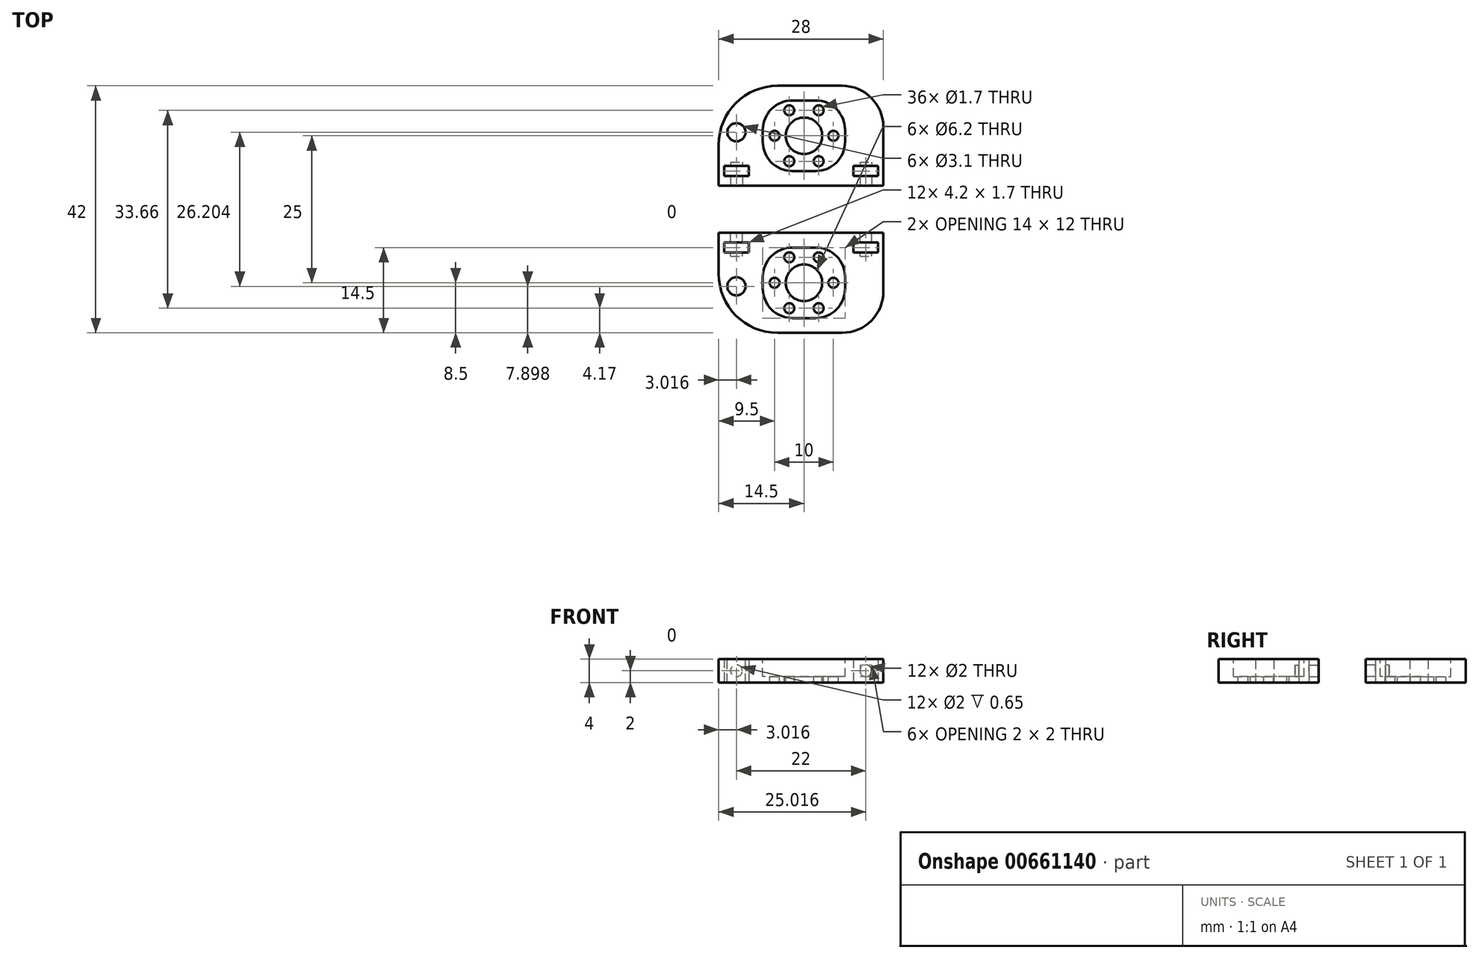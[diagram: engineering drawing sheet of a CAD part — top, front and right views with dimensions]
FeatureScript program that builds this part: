
annotation { "Feature Type Name" : "Feature", "Feature Type Description" : "" }
export const myFeature = defineFeature(function(context is Context, id is Id, definition is map)
    precondition{}
    {
        {
            var Q0;
            Q0=qCreatedBy(makeId("Front.planeOp"),FACE);
            var sketch = newSketch(context, id + "F0", { "sketchPlane" : qUnion([Q0])});
            skLineSegment(sketch, "E0.bottom", {"start": v(0, 0) * mm, "end": v(28, 0) * mm});
            skLineSegment(sketch, "E0.top", {"start": v(0, 17) * mm, "end": v(28, 17) * mm});
            skLineSegment(sketch, "E0.left", {"start": v(0, 0) * mm, "end": v(0, 17) * mm});
            skLineSegment(sketch, "E0.right", {"start": v(28, 0) * mm, "end": v(28, 17) * mm});
            skCircle(sketch, "E1", {"center": v(14.5, 8.5) * mm, "radius": 3.1 * mm});
            skCircle(sketch, "E2", {"center": v(19.5, 8.5) * mm, "radius": 0.85 * mm});
            skCircle(sketch, "E3.1.0", {"center": v(17, 12.83) * mm, "radius": 0.85 * mm});
            skCircle(sketch, "E3.2.0", {"center": v(12, 12.83) * mm, "radius": 0.85 * mm});
            skCircle(sketch, "E3.3.0", {"center": v(9.5, 8.5) * mm, "radius": 0.85 * mm});
            skCircle(sketch, "E3.4.0", {"center": v(12, 4.17) * mm, "radius": 0.85 * mm});
            skCircle(sketch, "E3.5.0", {"center": v(17, 4.17) * mm, "radius": 0.85 * mm});
            skLineSegment(sketch, "E4.bottom", {"start": v(7.5, 14.5) * mm, "end": v(21.5, 14.5) * mm});
            skLineSegment(sketch, "E4.top", {"start": v(7.5, 2.5) * mm, "end": v(21.5, 2.5) * mm});
            skLineSegment(sketch, "E4.left", {"start": v(7.5, 14.5) * mm, "end": v(7.5, 2.5) * mm});
            skLineSegment(sketch, "E4.right", {"start": v(21.5, 14.5) * mm, "end": v(21.5, 2.5) * mm});
            skCircle(sketch, "E5", {"center": v(3.02, 9.1) * mm, "radius": 1.55 * mm});
            skLineSegment(sketch, "E6", {"start": v(3.02, 9.1) * mm, "end": v(14.5, 8.5) * mm});
            skLineSegment(sketch, "E7", {"start": v(14.5, 8.5) * mm, "end": v(0, 8.5) * mm});
            skSolve(sketch);
        }
        {
            var Q0;
            Q0=makeQuery(id+"F0.imprint","IMPRINT",FACE,{"disambiguationData":[TD([[makeQuery(id+"F0.imprint","IMPRINT",EDGE,{"derivedFrom":sQuery(id+"F0.wireOp",EDGE,"E0.bottom")}),1.0]])]});
            var Q1;
            Q1=makeQuery(id+"F0.imprint","IMPRINT",FACE,{"disambiguationData":[TD([[makeQuery(id+"F0.imprint","IMPRINT",EDGE,{"derivedFrom":sQuery(id+"F0.wireOp",EDGE,"E1")}),-1.0]])]});
            var Q2;
            Q2=makeQuery(id+"F0.imprint","IMPRINT",FACE,{"disambiguationData":[TD([[makeQuery(id+"F0.imprint","IMPRINT",EDGE,{"derivedFrom":sQuery(id+"F0.wireOp",EDGE,"E2")}),-1.0]])]});
            var Q3;
            {var subQ0=sQuery(id+"F0.wireOp",EDGE,"E6");var subQ1=sQuery(id+"F0.wireOp",EDGE,"E3.3.0");var subQ2=makeQuery(id+"F0.imprint","INTERSECT",VERTEX,{"disambiguationData":[OD(0.0)],"derivedFrom":[subQ1,subQ0]});Q3=makeQuery(id+"F0.imprint","IMPRINT",FACE,{"disambiguationData":[TD([[makeQuery(id+"F0.imprint","IMPRINT",EDGE,{"disambiguationData":[TD([[subQ2,1.0]])],"derivedFrom":subQ1}),-1.0]])]});}
            var Q4;
            {var subQ0=sQuery(id+"F0.wireOp",EDGE,"E7");var subQ1=sQuery(id+"F0.wireOp",EDGE,"E4.left");var subQ2=makeQuery(id+"F0.imprint","INTERSECT",VERTEX,{"derivedFrom":[subQ1,subQ0]});Q4=makeQuery(id+"F0.imprint","IMPRINT",FACE,{"disambiguationData":[TD([[makeQuery(id+"F0.imprint","IMPRINT",EDGE,{"disambiguationData":[TD([[subQ2,-1.0]])],"derivedFrom":subQ1}),-1.0]])]});}
            var Q5;
            {var subQ0=sQuery(id+"F0.wireOp",EDGE,"E6");var subQ1=sQuery(id+"F0.wireOp",EDGE,"E4.left");var subQ2=makeQuery(id+"F0.imprint","INTERSECT",VERTEX,{"derivedFrom":[subQ1,subQ0]});Q5=makeQuery(id+"F0.imprint","IMPRINT",FACE,{"disambiguationData":[TD([[makeQuery(id+"F0.imprint","IMPRINT",EDGE,{"disambiguationData":[TD([[subQ2,-1.0]])],"derivedFrom":subQ1}),-1.0]])]});}
            var Q6;
            {var subQ0=sQuery(id+"F0.wireOp",EDGE,"E6");var subQ1=sQuery(id+"F0.wireOp",EDGE,"E3.3.0");var subQ2=makeQuery(id+"F0.imprint","INTERSECT",VERTEX,{"disambiguationData":[OD(1.0)],"derivedFrom":[subQ1,subQ0]});Q6=makeQuery(id+"F0.imprint","IMPRINT",FACE,{"disambiguationData":[TD([[makeQuery(id+"F0.imprint","IMPRINT",EDGE,{"disambiguationData":[TD([[subQ2,-1.0]])],"derivedFrom":subQ1}),-1.0]])]});}
            extrude(context, id + "F1", {"entities" : qUnion([Q0, Q1, Q2, Q3, Q4, Q5, Q6]), "depth" : 4 * mm});
        }
        {
            var Q0;
            Q0=makeQuery(id+"F1.opExtrude","SWEPT_EDGE",EDGE,{"disambiguationData":[OSD([sQuery(id+"F0.wireOp",EDGE,"E0.top"),sQuery(id+"F0.wireOp",EDGE,"E0.left")])]});
            fillet(context, id + "F2", {"entities" : qUnion([Q0]), "radius" : 10 * mm, "tangentPropagation" : true, "allowEdgeOverflow" : false});
        }
        {
            var Q0;
            Q0=makeQuery(id+"F0.imprint","IMPRINT",FACE,{"disambiguationData":[TD([[makeQuery(id+"F0.imprint","IMPRINT",EDGE,{"derivedFrom":sQuery(id+"F0.wireOp",EDGE,"E2")}),-1.0]])]});
            var Q1;
            {var subQ0=sQuery(id+"F0.wireOp",EDGE,"E6");var subQ1=sQuery(id+"F0.wireOp",EDGE,"E1");var subQ2=makeQuery(id+"F0.imprint","INTERSECT",VERTEX,{"derivedFrom":[subQ1,subQ0]});Q1=makeQuery(id+"F0.imprint","IMPRINT",FACE,{"disambiguationData":[TD([[makeQuery(id+"F0.imprint","IMPRINT",EDGE,{"disambiguationData":[TD([[subQ2,1.0]])],"derivedFrom":subQ1}),-1.0]])]});}
            var Q2;
            {var subQ0=sQuery(id+"F0.wireOp",EDGE,"E6");var subQ1=sQuery(id+"F0.wireOp",EDGE,"E3.3.0");var subQ2=makeQuery(id+"F0.imprint","INTERSECT",VERTEX,{"disambiguationData":[OD(1.0)],"derivedFrom":[subQ1,subQ0]});Q2=makeQuery(id+"F0.imprint","IMPRINT",FACE,{"disambiguationData":[TD([[makeQuery(id+"F0.imprint","IMPRINT",EDGE,{"disambiguationData":[TD([[subQ2,-1.0]])],"derivedFrom":subQ1}),-1.0]])]});}
            var Q3;
            {var subQ0=sQuery(id+"F0.wireOp",EDGE,"E6");var subQ1=sQuery(id+"F0.wireOp",EDGE,"E1");var subQ2=makeQuery(id+"F0.imprint","INTERSECT",VERTEX,{"derivedFrom":[subQ1,subQ0]});Q3=makeQuery(id+"F0.imprint","IMPRINT",FACE,{"disambiguationData":[TD([[makeQuery(id+"F0.imprint","IMPRINT",EDGE,{"disambiguationData":[TD([[subQ2,-1.0]])],"derivedFrom":subQ1}),-1.0]])]});}
            extrude(context, id + "F3", {"entities" : qUnion([Q0, Q1, Q2, Q3]), "operationType" : NewBodyOperationType.REMOVE, "depth" : 3 * mm});
        }
        {
            var Q0;
            Q0=makeQuery(id+"F3.boolean.opBoolean","COPY",EDGE,{"derivedFrom":makeQuery(id+"F3.opExtrude","SWEPT_EDGE",EDGE,{"disambiguationData":[OSD([sQuery(id+"F0.wireOp",EDGE,"E4.bottom"),sQuery(id+"F0.wireOp",EDGE,"E4.right")])]})});
            var Q1;
            Q1=makeQuery(id+"F3.boolean.opBoolean","COPY",EDGE,{"derivedFrom":makeQuery(id+"F3.opExtrude","SWEPT_EDGE",EDGE,{"disambiguationData":[OSD([sQuery(id+"F0.wireOp",EDGE,"E4.top"),sQuery(id+"F0.wireOp",EDGE,"E4.right")])]})});
            var Q2;
            Q2=makeQuery(id+"F3.boolean.opBoolean","COPY",EDGE,{"derivedFrom":makeQuery(id+"F3.opExtrude","SWEPT_EDGE",EDGE,{"disambiguationData":[OSD([sQuery(id+"F0.wireOp",EDGE,"E4.top"),sQuery(id+"F0.wireOp",EDGE,"E4.left")])]})});
            var Q3;
            Q3=makeQuery(id+"F3.boolean.opBoolean","COPY",EDGE,{"derivedFrom":makeQuery(id+"F3.opExtrude","SWEPT_EDGE",EDGE,{"disambiguationData":[OSD([sQuery(id+"F0.wireOp",EDGE,"E4.bottom"),sQuery(id+"F0.wireOp",EDGE,"E4.left")])]})});
            fillet(context, id + "F4", {"entities" : qUnion([Q0, Q1, Q2, Q3]), "radius" : 5 * mm, "tangentPropagation" : true, "allowEdgeOverflow" : false});
        }
        {
            var Q0;
            Q0=makeQuery(id+"F1.opExtrude","SWEPT_EDGE",EDGE,{"disambiguationData":[OSD([sQuery(id+"F0.wireOp",EDGE,"E0.top"),sQuery(id+"F0.wireOp",EDGE,"E0.right")])]});
            fillet(context, id + "F5", {"entities" : qUnion([Q0]), "radius" : 7 * mm, "tangentPropagation" : true, "allowEdgeOverflow" : false});
        }
        {
            var Q0;
            Q0=makeQuery(id+"F1.opExtrude","SWEPT_FACE",FACE,{"disambiguationData":[OSD([sQuery(id+"F0.wireOp",EDGE,"E0.bottom")])]});
            var sketch = newSketch(context, id + "F6", { "sketchPlane" : qUnion([Q0])});
            skCircle(sketch, "E8", {"center": v(3.02, 2) * mm, "radius": 1 * mm});
            skCircle(sketch, "E9", {"center": v(25.02, 2) * mm, "radius": 1 * mm});
            skSolve(sketch);
        }
        {
            var Q0;
            Q0=qSketchRegion(id+"F6",true);
            extrude(context, id + "F7", {"entities" : qUnion([Q0]), "operationType" : NewBodyOperationType.REMOVE, "oppositeDirection" : true, "depth" : 4 * mm});
        }
        {
            var Q0;
            Q0=makeQuery(id+"F1.opExtrude","CAP_FACE",FACE,{"disambiguationData":[OSD([sQuery(id+"F0.wireOp",EDGE,"E0.bottom"),sQuery(id+"F0.wireOp",EDGE,"E0.top"),sQuery(id+"F0.wireOp",EDGE,"E0.left"),sQuery(id+"F0.wireOp",EDGE,"E0.right"),sQuery(id+"F0.wireOp",EDGE,"wE7doQa1-f1d0-D7SE-Vx9v-5G1ykLdNQw0D"),sQuery(id+"F0.wireOp",EDGE,"E1"),sQuery(id+"F0.wireOp",EDGE,"E2"),sQuery(id+"F0.wireOp",EDGE,"E3.1.0"),sQuery(id+"F0.wireOp",EDGE,"E3.2.0"),sQuery(id+"F0.wireOp",EDGE,"E3.3.0"),sQuery(id+"F0.wireOp",EDGE,"E3.4.0"),sQuery(id+"F0.wireOp",EDGE,"E3.5.0")])],"isStart":false});
            var sketch = newSketch(context, id + "F8", { "sketchPlane" : qUnion([Q0])});
            skLineSegment(sketch, "E10.bottom", {"start": v(0.92, 3.35) * mm, "end": v(5.12, 3.35) * mm});
            skLineSegment(sketch, "E10.top", {"start": v(0.92, 1.65) * mm, "end": v(5.12, 1.65) * mm});
            skLineSegment(sketch, "E10.left", {"start": v(0.92, 3.35) * mm, "end": v(0.92, 1.65) * mm});
            skLineSegment(sketch, "E10.right", {"start": v(5.12, 3.35) * mm, "end": v(5.12, 1.65) * mm});
            skPoint(sketch, "E10.middle", {"position": v(3.02, 2.5) * mm});
            skLineSegment(sketch, "E11.bottom", {"start": v(27.12, 3.35) * mm, "end": v(22.92, 3.35) * mm});
            skLineSegment(sketch, "E11.top", {"start": v(27.12, 1.65) * mm, "end": v(22.92, 1.65) * mm});
            skLineSegment(sketch, "E11.left", {"start": v(27.12, 3.35) * mm, "end": v(27.12, 1.65) * mm});
            skLineSegment(sketch, "E11.right", {"start": v(22.92, 3.35) * mm, "end": v(22.92, 1.65) * mm});
            skPoint(sketch, "E11.middle", {"position": v(25.02, 2.5) * mm});
            skSolve(sketch);
        }
        {
            var Q0;
            Q0=qSketchRegion(id+"F8",true);
            extrude(context, id + "F9", {"entities" : qUnion([Q0]), "operationType" : NewBodyOperationType.REMOVE, "oppositeDirection" : true, "depth" : 4 * mm});
        }
        {
            var Q0;
            Q0=makeQuery(id+"F1.opExtrude","SWEPT_BODY",BODY,{"disambiguationData":[OSD([sQuery(id+"F0.wireOp",EDGE,"E0.bottom"),sQuery(id+"F0.wireOp",EDGE,"E0.top"),sQuery(id+"F0.wireOp",EDGE,"E0.left"),sQuery(id+"F0.wireOp",EDGE,"E0.right"),sQuery(id+"F0.wireOp",EDGE,"E1"),sQuery(id+"F0.wireOp",EDGE,"E2"),sQuery(id+"F0.wireOp",EDGE,"E3.1.0"),sQuery(id+"F0.wireOp",EDGE,"E3.2.0"),sQuery(id+"F0.wireOp",EDGE,"E3.3.0"),sQuery(id+"F0.wireOp",EDGE,"E3.4.0"),sQuery(id+"F0.wireOp",EDGE,"E3.5.0"),sQuery(id+"F0.wireOp",EDGE,"E5")])]});
            var Q1;
            Q1=qCreatedBy(makeId("Right.planeOp"),FACE);
            transform(context, id + "F10", {"entities" : qUnion([Q0]), "transformType" : TransformType.TRANSLATION_DISTANCE, "transformDirection" : qUnion([Q1]), "distance" : 5 * mm, "makeCopy" : false});
        }
        {
            var Q0;
            Q0=makeQuery(id+"F1.opExtrude","SWEPT_BODY",BODY,{"disambiguationData":[OSD([sQuery(id+"F0.wireOp",EDGE,"E0.bottom"),sQuery(id+"F0.wireOp",EDGE,"E0.top"),sQuery(id+"F0.wireOp",EDGE,"E0.left"),sQuery(id+"F0.wireOp",EDGE,"E0.right"),sQuery(id+"F0.wireOp",EDGE,"E1"),sQuery(id+"F0.wireOp",EDGE,"E2"),sQuery(id+"F0.wireOp",EDGE,"E3.1.0"),sQuery(id+"F0.wireOp",EDGE,"E3.2.0"),sQuery(id+"F0.wireOp",EDGE,"E3.3.0"),sQuery(id+"F0.wireOp",EDGE,"E3.4.0"),sQuery(id+"F0.wireOp",EDGE,"E3.5.0"),sQuery(id+"F0.wireOp",EDGE,"E5")])]});
            var Q1;
            Q1=makeQuery(id+"F1.opExtrude","CAP_EDGE",EDGE,{"disambiguationData":[OSD([sQuery(id+"F0.wireOp",EDGE,"E0.bottom")])],"isStart":false});
            transform(context, id + "F11", {"entities" : qUnion([Q0]), "transformType" : TransformType.ROTATION, "transformAxis" : qUnion([Q1]), "angle" : 90 * degree, "makeCopy" : false});
        }
        {
            var Q0;
            Q0=makeQuery(id+"F1.opExtrude","SWEPT_BODY",BODY,{"disambiguationData":[OSD([sQuery(id+"F0.wireOp",EDGE,"E0.bottom"),sQuery(id+"F0.wireOp",EDGE,"E0.top"),sQuery(id+"F0.wireOp",EDGE,"E0.left"),sQuery(id+"F0.wireOp",EDGE,"E0.right"),sQuery(id+"F0.wireOp",EDGE,"E1"),sQuery(id+"F0.wireOp",EDGE,"E2"),sQuery(id+"F0.wireOp",EDGE,"E3.1.0"),sQuery(id+"F0.wireOp",EDGE,"E3.2.0"),sQuery(id+"F0.wireOp",EDGE,"E3.3.0"),sQuery(id+"F0.wireOp",EDGE,"E3.4.0"),sQuery(id+"F0.wireOp",EDGE,"E3.5.0"),sQuery(id+"F0.wireOp",EDGE,"E5")])]});
            var Q1;
            Q1=qCreatedBy(makeId("Front.planeOp"),FACE);
            mirror(context, id + "F12", {"entities" : qUnion([Q0]), "mirrorPlane" : qUnion([Q1])});
        }
    });
